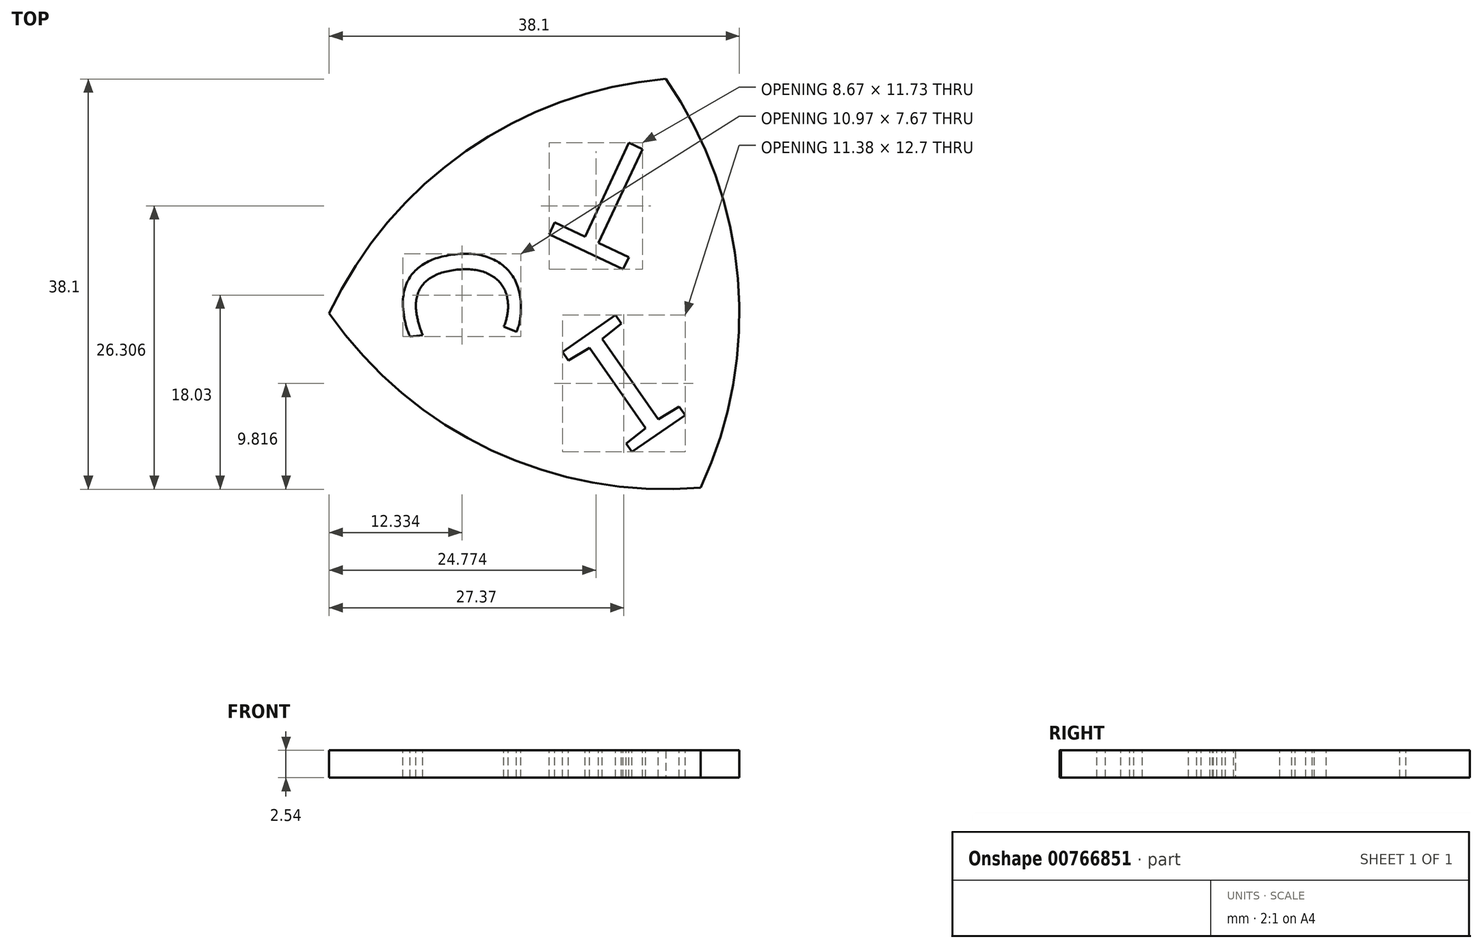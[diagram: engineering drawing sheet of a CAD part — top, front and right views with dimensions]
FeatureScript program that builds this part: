
annotation { "Feature Type Name" : "Feature", "Feature Type Description" : "" }
export const myFeature = defineFeature(function(context is Context, id is Id, definition is map)
    precondition{}
    {
        {
            var Q0;
            Q0=qCreatedBy(makeId("Top.planeOp"),FACE);
            var sketch = newSketch(context, id + "F0", { "sketchPlane" : qUnion([Q0])});
            skCircle(sketch, "E0", {"center": v(0, 0) * mm, "radius": 38.1 * mm});
            skSolve(sketch);
        }
        {
            var Q0;
            Q0=qCreatedBy(makeId("Top.planeOp"),FACE);
            var sketch = newSketch(context, id + "F1", { "sketchPlane" : qUnion([Q0])});
            skCircle(sketch, "E1", {"center": v(-34.49, 16.2) * mm, "radius": 38.1 * mm});
            skSolve(sketch);
        }
        {
            var Q0;
            Q0=qCreatedBy(makeId("Top.planeOp"),FACE);
            var sketch = newSketch(context, id + "F2", { "sketchPlane" : qUnion([Q0])});
            skCircle(sketch, "E2", {"center": v(-3.22, 37.96) * mm, "radius": 38.1 * mm});
            skSolve(sketch);
        }
        {
            var Q0;
            Q0=makeQuery(id+"F0.imprint","IMPRINT",FACE,{"disambiguationData":[TD([[makeQuery(id+"F0.imprint","IMPRINT",EDGE,{"derivedFrom":sQuery(id+"F0.wireOp",EDGE,"E0")}),1.0]])]});
            var Q1;
            Q1 = qSketchRegion(id + "F0", true);
            extrude(context, id + "F3", {"entities" : qUnion([Q0, Q1]), "depth" : 2.54 * mm, "offsetDistance" : 25.4 * mm});
        }
        {
            var Q0;
            Q0 = qSketchRegion(id + "F1", true);
            extrude(context, id + "F4", {"entities" : qUnion([Q0]), "operationType" : NewBodyOperationType.INTERSECT, "depth" : 2.54 * mm, "offsetDistance" : 25.4 * mm});
        }
        {
            var Q0;
            Q0 = qSketchRegion(id + "F2", true);
            extrude(context, id + "F5", {"entities" : qUnion([Q0]), "operationType" : NewBodyOperationType.INTERSECT, "depth" : 2.54 * mm, "offsetDistance" : 25.4 * mm});
        }
        {
            var Q0;
            Q0=makeQuery(id+"F3.opExtrude","CAP_FACE",FACE,{"disambiguationData":[OSD([sQuery(id+"F0.wireOp",EDGE,"E0")])],"isStart":false});
            var sketch = newSketch(context, id + "F6", { "sketchPlane" : qUnion([Q0])});
            skText(sketch, "E3", { "text": "T", "fontName": "DroidSansMono.ttf"});
            skLineSegment(sketch, "E4", {"start": v(0, 0) * mm, "end": v(-34.49, 16.2) * mm, "construction": true});
            skLineSegment(sketch, "E5", {"start": v(-17.24, 8.1) * mm, "end": v(-3.22, 37.96) * mm, "construction": true});
            const initialGuessF6  = {"E3": [-0.00189, 0.0298, -0.90515, 0.4251, 0.01094]};
            skSetInitialGuess(sketch, initialGuessF6);
            skSolve(sketch);
        }
        {
            var Q0;
            Q0 = qSketchRegion(id + "F6", true);
            extrude(context, id + "F7", {"entities" : qUnion([Q0]), "operationType" : NewBodyOperationType.REMOVE, "oppositeDirection" : true, "depth" : 25.4 * mm, "offsetDistance" : 25.4 * mm});
        }
        {
            var Q0;
            Q0=makeQuery(id+"F3.opExtrude","CAP_FACE",FACE,{"disambiguationData":[OSD([sQuery(id+"F0.wireOp",EDGE,"E0")])],"isStart":false});
            var sketch = newSketch(context, id + "F8", { "sketchPlane" : qUnion([Q0])});
            skLineSegment(sketch, "E6", {"start": v(0, 0) * mm, "end": v(-3.22, 37.96) * mm, "construction": true});
            skLineSegment(sketch, "E7", {"start": v(-34.49, 16.2) * mm, "end": v(-1.6, 18.98) * mm, "construction": true});
            skText(sketch, "E8", { "text": "C", "fontName": "DroidSansMono.ttf"});
            const initialGuessF8  = {"E8": [-0.02794, 0.02218, 0.08443, -0.99643, 0.01073]};
            skSetInitialGuess(sketch, initialGuessF8);
            skSolve(sketch);
        }
        {
            var Q0;
            Q0 = qSketchRegion(id + "F8", true);
            extrude(context, id + "F9", {"entities" : qUnion([Q0]), "operationType" : NewBodyOperationType.REMOVE, "oppositeDirection" : true, "depth" : 25.4 * mm, "offsetDistance" : 25.4 * mm});
        }
        {
            var Q0;
            Q0=makeQuery(id+"F3.opExtrude","CAP_FACE",FACE,{"disambiguationData":[OSD([sQuery(id+"F0.wireOp",EDGE,"E0")])],"isStart":false});
            var sketch = newSketch(context, id + "F10", { "sketchPlane" : qUnion([Q0])});
            skText(sketch, "E9", { "text": "I", "fontName": "DroidSansMono.ttf"});
            skLineSegment(sketch, "E10", {"start": v(-34.49, 16.2) * mm, "end": v(-3.22, 37.96) * mm, "construction": true});
            skLineSegment(sketch, "E11", {"start": v(0, 0) * mm, "end": v(-18.85, 27.08) * mm, "construction": true});
            const initialGuessF10  = {"E9": [-0.00778, 0.00233, 0.82072, 0.57133, 0.0114]};
            skSetInitialGuess(sketch, initialGuessF10);
            skSolve(sketch);
        }
        {
            var Q0;
            Q0 = qSketchRegion(id + "F10", true);
            extrude(context, id + "F11", {"entities" : qUnion([Q0]), "operationType" : NewBodyOperationType.REMOVE, "oppositeDirection" : true, "depth" : 25.4 * mm, "offsetDistance" : 25.4 * mm});
        }
    });
